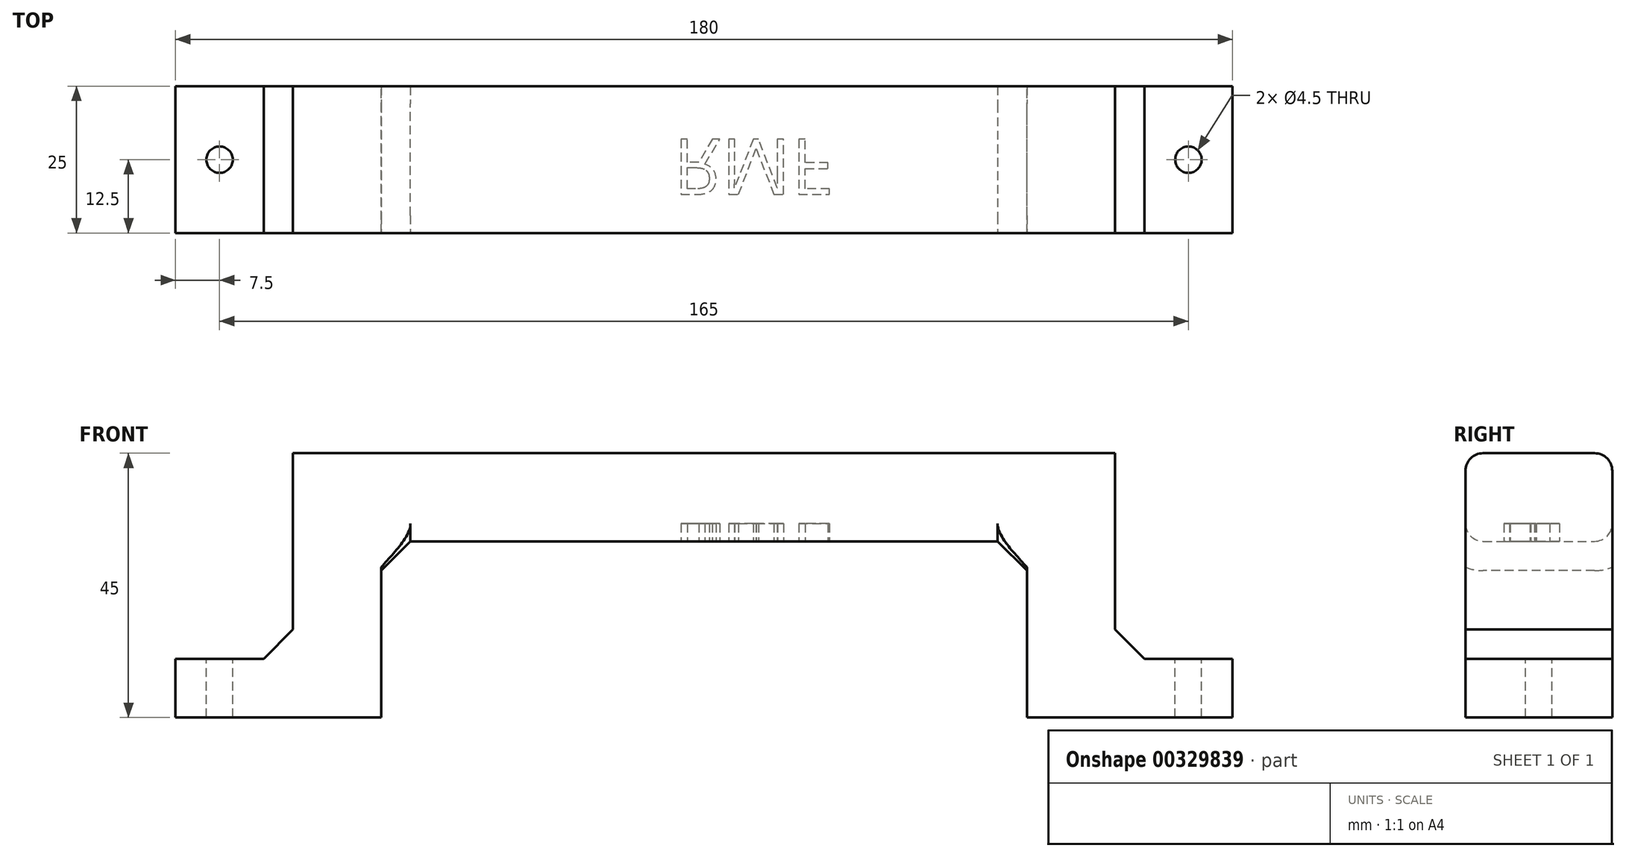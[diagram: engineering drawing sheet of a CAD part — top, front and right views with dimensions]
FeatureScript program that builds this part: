
annotation { "Feature Type Name" : "Feature", "Feature Type Description" : "" }
export const myFeature = defineFeature(function(context is Context, id is Id, definition is map)
    precondition{}
    {
        {
            var Q0;
            Q0=qCreatedBy(makeId("Front.planeOp"),FACE);
            var sketch = newSketch(context, id + "F0", { "sketchPlane" : qUnion([Q0])});
            skLineSegment(sketch, "E0", {"start": v(0, 0) * mm, "end": v(35, 0) * mm});
            skLineSegment(sketch, "E1", {"start": v(35, 0) * mm, "end": v(35, 30) * mm});
            skLineSegment(sketch, "E2", {"start": v(35, 30) * mm, "end": v(90, 30) * mm});
            skLineSegment(sketch, "E3", {"start": v(90, 30) * mm, "end": v(90, 45) * mm, "construction": true});
            skLineSegment(sketch, "E4", {"start": v(90, 45) * mm, "end": v(20, 45) * mm});
            skLineSegment(sketch, "E5", {"start": v(20, 45) * mm, "end": v(20, 10) * mm});
            skLineSegment(sketch, "E6", {"start": v(20, 10) * mm, "end": v(0, 10) * mm});
            skLineSegment(sketch, "E7", {"start": v(0, 10) * mm, "end": v(0, 0) * mm});
            skLineSegment(sketch, "E8.MirrorCS", {"start": v(90, 45) * mm, "end": v(160, 45) * mm});
            skLineSegment(sketch, "E9.MirrorCS", {"start": v(145, 30) * mm, "end": v(90, 30) * mm});
            skLineSegment(sketch, "E10.MirrorCS", {"start": v(145, 0) * mm, "end": v(145, 30) * mm});
            skLineSegment(sketch, "E11.MirrorCS", {"start": v(160, 45) * mm, "end": v(160, 10) * mm});
            skLineSegment(sketch, "E12.MirrorCS", {"start": v(160, 10) * mm, "end": v(180, 10) * mm});
            skLineSegment(sketch, "E13.MirrorCS", {"start": v(180, 10) * mm, "end": v(180, 0) * mm});
            skLineSegment(sketch, "E14.MirrorCS", {"start": v(180, 0) * mm, "end": v(145, 0) * mm});
            skSolve(sketch);
        }
        {
            var Q0;
            Q0=makeQuery(id+"F0.imprint","IMPRINT",FACE,{"disambiguationData":[TD([[makeQuery(id+"F0.imprint","IMPRINT",EDGE,{"derivedFrom":sQuery(id+"F0.wireOp",EDGE,"E0")}),1.0]])]});
            extrude(context, id + "F1", {"entities" : qUnion([Q0]), "depth" : 25 * mm, "offsetDistance" : 25 * mm});
        }
        {
            var Q0;
            Q0=makeQuery(id+"F1.opExtrude","CAP_EDGE",EDGE,{"disambiguationData":[OSD([sQuery(id+"F0.wireOp",EDGE,"E4"),sQuery(id+"F0.wireOp",EDGE,"E8.MirrorCS")])],"isStart":false});
            var Q1;
            Q1=makeQuery(id+"F1.opExtrude","CAP_EDGE",EDGE,{"disambiguationData":[OSD([sQuery(id+"F0.wireOp",EDGE,"E4"),sQuery(id+"F0.wireOp",EDGE,"E8.MirrorCS")])],"isStart":true});
            var Q2;
            Q2=makeQuery(id+"F1.opExtrude","CAP_EDGE",EDGE,{"disambiguationData":[OSD([sQuery(id+"F0.wireOp",EDGE,"E2"),sQuery(id+"F0.wireOp",EDGE,"E9.MirrorCS")])],"isStart":false});
            var Q3;
            Q3=makeQuery(id+"F1.opExtrude","CAP_EDGE",EDGE,{"disambiguationData":[OSD([sQuery(id+"F0.wireOp",EDGE,"E2"),sQuery(id+"F0.wireOp",EDGE,"E9.MirrorCS")])],"isStart":true});
            fillet(context, id + "F2", {"entities" : qUnion([Q0, Q1, Q2, Q3]), "radius" : 3 * mm, "tangentPropagation" : true, "allowEdgeOverflow" : false});
        }
        {
            var Q0;
            Q0=makeQuery(id+"F1.opExtrude","SWEPT_EDGE",EDGE,{"disambiguationData":[OSD([sQuery(id+"F0.wireOp",EDGE,"E5"),sQuery(id+"F0.wireOp",EDGE,"E6")])]});
            var Q1;
            Q1=makeQuery(id+"F1.opExtrude","SWEPT_EDGE",EDGE,{"disambiguationData":[OSD([sQuery(id+"F0.wireOp",EDGE,"E11.MirrorCS"),sQuery(id+"F0.wireOp",EDGE,"E12.MirrorCS")])]});
            var Q2;
            Q2=makeQuery(id+"F1.opExtrude","SWEPT_EDGE",EDGE,{"disambiguationData":[OSD([sQuery(id+"F0.wireOp",EDGE,"E1"),sQuery(id+"F0.wireOp",EDGE,"E2")])]});
            var Q3;
            Q3=makeQuery(id+"F1.opExtrude","SWEPT_EDGE",EDGE,{"disambiguationData":[OSD([sQuery(id+"F0.wireOp",EDGE,"E9.MirrorCS"),sQuery(id+"F0.wireOp",EDGE,"E10.MirrorCS")])]});
            chamfer(context, id + "F3", {"entities" : qUnion([Q0, Q1, Q2, Q3]), "width" : 5 * mm, "tangentPropagation" : true});
        }
        {
            var Q0;
            Q0=makeQuery(id+"F1.opExtrude","SWEPT_FACE",FACE,{"disambiguationData":[OSD([sQuery(id+"F0.wireOp",EDGE,"E6")])]});
            var sketch = newSketch(context, id + "F4", { "sketchPlane" : qUnion([Q0])});
            skCircle(sketch, "E15", {"center": v(7.5, -12.5) * mm, "radius": 2.25 * mm});
            skPoint(sketch, "E15.centerSnap0", {"position": v(7.5, 0) * mm});
            skPoint(sketch, "E15.centerSnap1", {"position": v(0, -12.5) * mm});
            skLineSegment(sketch, "E16", {"start": v(90, 0) * mm, "end": v(90, -25) * mm, "construction": true});
            skCircle(sketch, "E17.MirrorC", {"center": v(172.5, -12.5) * mm, "radius": 2.25 * mm});
            skSolve(sketch);
        }
        {
            var Q0;
            Q0 = qSketchRegion(id + "F4", true);
            extrude(context, id + "F5", {"entities" : qUnion([Q0]), "operationType" : NewBodyOperationType.REMOVE, "endBound" : BoundingType.THROUGH_ALL, "oppositeDirection" : true, "depth" : 25 * mm, "offsetDistance" : 25 * mm});
        }
        {
            var Q0;
            Q0=makeQuery(id+"F1.opExtrude","SWEPT_FACE",FACE,{"disambiguationData":[OSD([sQuery(id+"F0.wireOp",EDGE,"E2"),sQuery(id+"F0.wireOp",EDGE,"E9.MirrorCS")])]});
            var sketch = newSketch(context, id + "F6", { "sketchPlane" : qUnion([Q0])});
            skText(sketch, "E18", { "text": "RMF", "fontName": "OpenSans-Regular.ttf"});
            const initialGuessF6  = {"E18": [0.08477, 0.00901, 1, 0, 0.0095]};
            skSetInitialGuess(sketch, initialGuessF6);
            skSolve(sketch);
        }
        {
            var Q0;
            Q0 = qSketchRegion(id + "F6", true);
            extrude(context, id + "F7", {"entities" : qUnion([Q0]), "operationType" : NewBodyOperationType.REMOVE, "oppositeDirection" : true, "depth" : 3 * mm, "offsetDistance" : 25 * mm});
        }
    });
